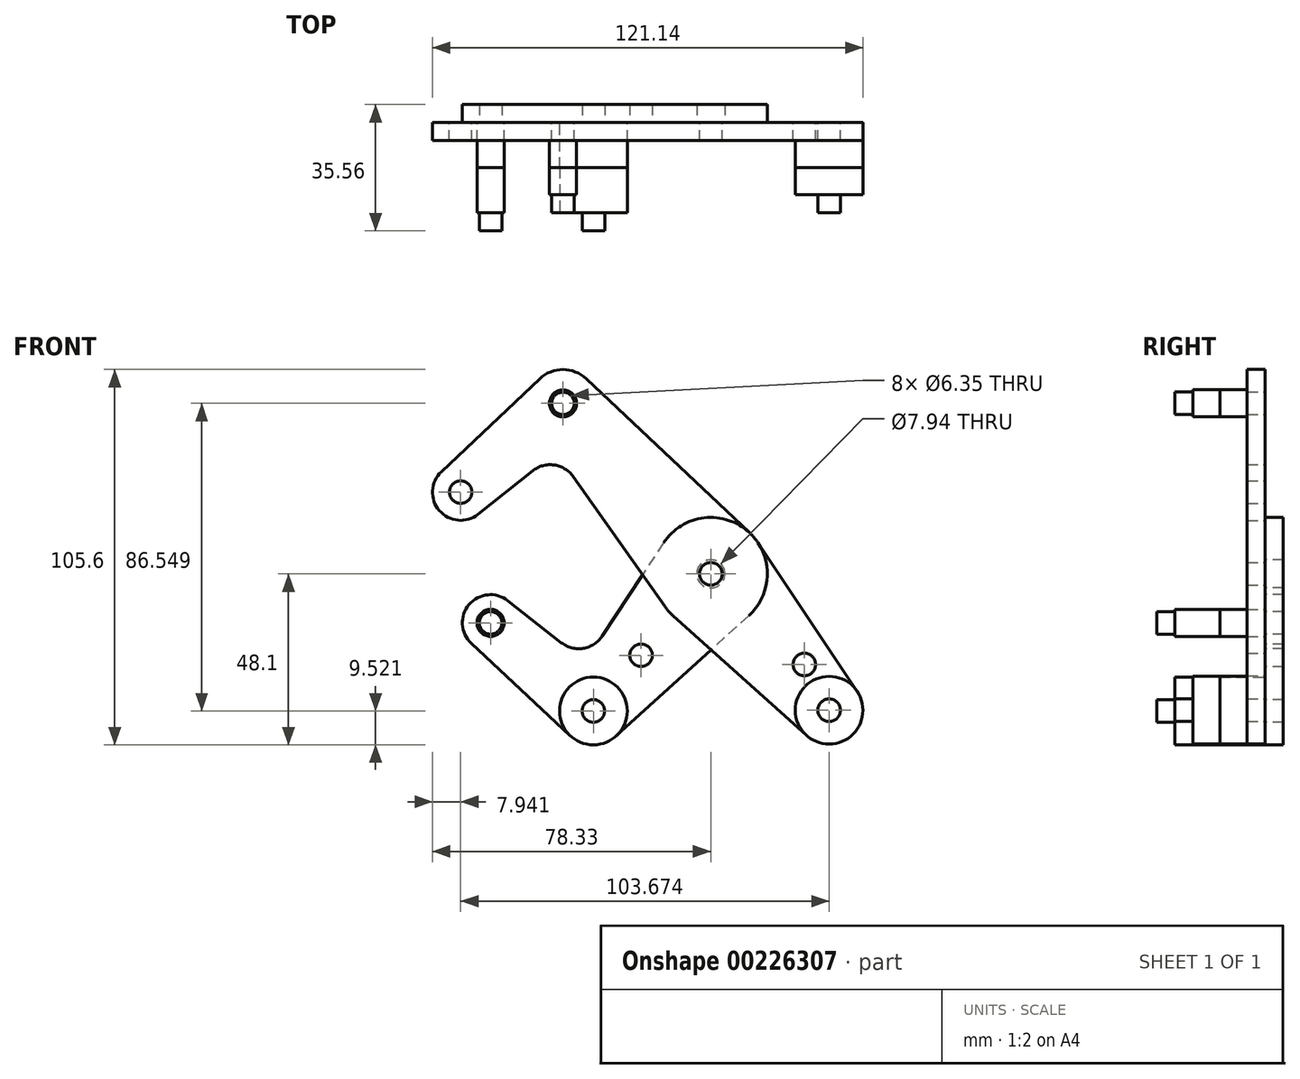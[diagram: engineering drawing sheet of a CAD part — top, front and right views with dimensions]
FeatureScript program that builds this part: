
annotation { "Feature Type Name" : "Feature", "Feature Type Description" : "" }
export const myFeature = defineFeature(function(context is Context, id is Id, definition is map)
    precondition{}
    {
        {
            var Q0;
            Q0=qCreatedBy(makeId("Front.planeOp"),FACE);
            var sketch = newSketch(context, id + "F0", { "sketchPlane" : qUnion([Q0])});
            skLineSegment(sketch, "E0", {"start": v(-41.6, 47.97) * mm, "end": v(41.6, -47.97) * mm, "construction": true});
            skCircle(sketch, "E1", {"center": v(0, 0) * mm, "radius": 3.18 * mm});
            skCircle(sketch, "E2", {"center": v(33.29, -38.38) * mm, "radius": 3.18 * mm});
            skCircle(sketch, "E3", {"center": v(-41.6, 47.97) * mm, "radius": 3.18 * mm});
            skCircle(sketch, "E4", {"center": v(-70.39, 23) * mm, "radius": 3.18 * mm});
            skLineSegment(sketch, "E5", {"start": v(-41.6, 47.97) * mm, "end": v(-70.39, 23) * mm, "construction": true});
            skCircle(sketch, "E6", {"center": v(33.29, -38.38) * mm, "radius": 9.53 * mm});
            skCircle(sketch, "E7", {"center": v(-70.39, 23) * mm, "radius": 7.94 * mm});
            skCircle(sketch, "E8", {"center": v(-41.6, 47.97) * mm, "radius": 9.53 * mm});
            skLineSegment(sketch, "E9", {"start": v(-75.83, 28.78) * mm, "end": v(-48.14, 54.9) * mm});
            skLineSegment(sketch, "E10", {"start": v(-65.44, 16.8) * mm, "end": v(-50.15, 28.98) * mm});
            skCircle(sketch, "E11", {"center": v(0, 0) * mm, "radius": 15.88 * mm});
            skLineSegment(sketch, "E12", {"start": v(-35.07, 54.9) * mm, "end": v(10.9, 11.55) * mm});
            skLineSegment(sketch, "E13", {"start": v(-38.72, 27.35) * mm, "end": v(-12.97, -9.15) * mm});
            skLineSegment(sketch, "E14", {"start": v(-10.6, -11.82) * mm, "end": v(26.93, -45.47) * mm});
            skLineSegment(sketch, "E15", {"start": v(13.2, 8.82) * mm, "end": v(41.2, -33.08) * mm});
            skArc(sketch, "E16.filletArc", {"start": v(-38.72, 27.35) * mm, "mid": v(-44.08, 30.63) * mm, "end": v(-50.15, 28.98) * mm});
            skLineSegment(sketch, "E17", {"start": v(0, 0) * mm, "end": v(-33.05, -38.58) * mm, "construction": true});
            skLineSegment(sketch, "E18", {"start": v(-33.05, -38.58) * mm, "end": v(-61.98, -13.8) * mm, "construction": true});
            skCircle(sketch, "E19", {"center": v(-61.98, -13.8) * mm, "radius": 3.18 * mm});
            skCircle(sketch, "E20", {"center": v(-33.05, -38.58) * mm, "radius": 3.18 * mm});
            skCircle(sketch, "E21", {"center": v(-61.98, -13.8) * mm, "radius": 7.94 * mm});
            skCircle(sketch, "E22", {"center": v(-33.05, -38.58) * mm, "radius": 9.53 * mm});
            skLineSegment(sketch, "E23", {"start": v(-57.08, -7.55) * mm, "end": v(-42.08, -19.35) * mm});
            skLineSegment(sketch, "E24", {"start": v(-67.4, -19.6) * mm, "end": v(-39.54, -45.55) * mm});
            skLineSegment(sketch, "E25", {"start": v(-13.25, 8.74) * mm, "end": v(-30.55, -17.48) * mm});
            skLineSegment(sketch, "E26", {"start": v(10.67, -11.75) * mm, "end": v(-26.65, -45.63) * mm});
            skArc(sketch, "E27.filletArc", {"start": v(-42.08, -19.35) * mm, "mid": v(-35.9, -20.95) * mm, "end": v(-30.55, -17.48) * mm});
            skCircle(sketch, "E28", {"center": v(-19.62, -22.9) * mm, "radius": 3.18 * mm});
            skCircle(sketch, "E29", {"center": v(26.32, -25.5) * mm, "radius": 3.18 * mm});
            skLineSegment(sketch, "E30", {"start": v(26.32, -25.5) * mm, "end": v(23.92, -27.58) * mm, "construction": true});
            skCircle(sketch, "E31", {"center": v(0, 0) * mm, "radius": 3.97 * mm});
            skSolve(sketch);
        }
        {
            var Q0;
            Q0=qCreatedBy(makeId("Front.planeOp"),FACE);
            cPlane(context, id + "F1", {"entities" : qUnion([Q0]), "cplaneType" : CPlaneType.OFFSET, "offset" : 12.7 * mm, "width" : 254 * mm, "height" : 254 * mm});
        }
        {
            var Q0;
            {var subQ1=sQuery(id+"F0.wireOp",EDGE,"E9");Q0=makeQuery(id+"F0.imprint","IMPRINT",FACE,{"disambiguationData":[TD([[makeQuery(id+"F0.imprint","IMPRINT",EDGE,{"derivedFrom":subQ1}),-1.0]])]});}
            var Q1;
            {var subQ0=sQuery(id+"F0.wireOp",EDGE,"E15");Q1=makeQuery(id+"F0.imprint","IMPRINT",FACE,{"disambiguationData":[TD([[makeQuery(id+"F0.imprint","IMPRINT",EDGE,{"derivedFrom":subQ0}),-1.0]])]});}
            var Q2;
            Q2=makeQuery(id+"F0.imprint","IMPRINT",FACE,{"disambiguationData":[TD([[makeQuery(id+"F0.imprint","IMPRINT",EDGE,{"derivedFrom":sQuery(id+"F0.wireOp",EDGE,"E2")}),-1.0]])]});
            var Q3;
            Q3=makeQuery(id+"F0.imprint","IMPRINT",FACE,{"disambiguationData":[TD([[makeQuery(id+"F0.imprint","IMPRINT",EDGE,{"derivedFrom":sQuery(id+"F0.wireOp",EDGE,"E31")}),-1.0]])]});
            var Q4;
            Q4=makeQuery(id+"F0.imprint","IMPRINT",FACE,{"disambiguationData":[TD([[makeQuery(id+"F0.imprint","IMPRINT",EDGE,{"derivedFrom":sQuery(id+"F0.wireOp",EDGE,"E3")}),-1.0]])]});
            var Q5;
            Q5=makeQuery(id+"F0.imprint","IMPRINT",FACE,{"disambiguationData":[TD([[makeQuery(id+"F0.imprint","IMPRINT",EDGE,{"derivedFrom":sQuery(id+"F0.wireOp",EDGE,"E4")}),-1.0]])]});
            var Q6;
            Q6=makeQuery(id+"F0.imprint","IMPRINT",FACE,{"disambiguationData":[TD([[makeQuery(id+"F0.imprint","IMPRINT",EDGE,{"derivedFrom":sQuery(id+"F0.wireOp",EDGE,"E1")}),-1.0]])]});
            var Q7;
            {var subQ0=sQuery(id+"F0.wireOp",EDGE,"E13");var subQ1=sQuery(id+"F0.wireOp",EDGE,"E11");var subQ2=makeQuery(id+"F0.imprint","INTERSECT",VERTEX,{"derivedFrom":[subQ1,subQ0]});Q7=makeQuery(id+"F0.imprint","IMPRINT",FACE,{"disambiguationData":[TD([[makeQuery(id+"F0.imprint","IMPRINT",EDGE,{"disambiguationData":[TD([[subQ2,1.0]])],"derivedFrom":subQ1}),-1.0]])]});}
            var Q8;
            {var subQ0=sQuery(id+"F0.wireOp",EDGE,"E14");var subQ1=sQuery(id+"F0.wireOp",EDGE,"E11");var subQ2=makeQuery(id+"F0.imprint","INTERSECT",VERTEX,{"derivedFrom":[subQ1,subQ0]});Q8=makeQuery(id+"F0.imprint","IMPRINT",FACE,{"disambiguationData":[TD([[makeQuery(id+"F0.imprint","IMPRINT",EDGE,{"disambiguationData":[TD([[subQ2,-1.0]])],"derivedFrom":subQ1}),-1.0]])]});}
            extrude(context, id + "F2", {"entities" : qUnion([Q0, Q1, Q2, Q3, Q4, Q5, Q6, Q7, Q8]), "depth" : 5.08 * mm});
        }
        {
            var Q0;
            {var subQ10=sQuery(id+"F0.wireOp",EDGE,"E23");Q0=makeQuery(id+"F0.imprint","IMPRINT",FACE,{"disambiguationData":[TD([[makeQuery(id+"F0.imprint","IMPRINT",EDGE,{"derivedFrom":subQ10}),-1.0]])]});}
            var Q1;
            Q1=makeQuery(id+"F0.imprint","IMPRINT",FACE,{"disambiguationData":[TD([[makeQuery(id+"F0.imprint","IMPRINT",EDGE,{"derivedFrom":sQuery(id+"F0.wireOp",EDGE,"E31")}),-1.0]])]});
            var Q2;
            {var subQ0=sQuery(id+"F0.wireOp",EDGE,"E13");var subQ1=sQuery(id+"F0.wireOp",EDGE,"E11");var subQ2=makeQuery(id+"F0.imprint","INTERSECT",VERTEX,{"derivedFrom":[subQ1,subQ0]});Q2=makeQuery(id+"F0.imprint","IMPRINT",FACE,{"disambiguationData":[TD([[makeQuery(id+"F0.imprint","IMPRINT",EDGE,{"disambiguationData":[TD([[subQ2,1.0]])],"derivedFrom":subQ1}),-1.0]])]});}
            var Q3;
            {var subQ0=sQuery(id+"F0.wireOp",EDGE,"E14");var subQ1=sQuery(id+"F0.wireOp",EDGE,"E11");var subQ2=makeQuery(id+"F0.imprint","INTERSECT",VERTEX,{"derivedFrom":[subQ1,subQ0]});Q3=makeQuery(id+"F0.imprint","IMPRINT",FACE,{"disambiguationData":[TD([[makeQuery(id+"F0.imprint","IMPRINT",EDGE,{"disambiguationData":[TD([[subQ2,-1.0]])],"derivedFrom":subQ1}),-1.0]])]});}
            var Q4;
            Q4=makeQuery(id+"F0.imprint","IMPRINT",FACE,{"disambiguationData":[TD([[makeQuery(id+"F0.imprint","IMPRINT",EDGE,{"derivedFrom":sQuery(id+"F0.wireOp",EDGE,"E20")}),-1.0]])]});
            var Q5;
            Q5=makeQuery(id+"F0.imprint","IMPRINT",FACE,{"disambiguationData":[TD([[makeQuery(id+"F0.imprint","IMPRINT",EDGE,{"derivedFrom":sQuery(id+"F0.wireOp",EDGE,"E19")}),-1.0]])]});
            extrude(context, id + "F3", {"entities" : qUnion([Q0, Q1, Q2, Q3, Q4, Q5]), "oppositeDirection" : true, "depth" : 5.08 * mm});
        }
        {
            var Q0;
            {var subQ1=sQuery(id+"F0.wireOp",EDGE,"E9");Q0=makeQuery(id+"F0.imprint","IMPRINT",FACE,{"disambiguationData":[TD([[makeQuery(id+"F0.imprint","IMPRINT",EDGE,{"derivedFrom":subQ1}),-1.0]])]});}
            var sketch = newSketch(context, id + "F4", { "sketchPlane" : qUnion([Q0])});
            skArc(sketch, "E32.0.0", {"start": v(26.93, -45.47) * mm, "mid": v(39.53, -45.57) * mm, "end": v(41.2, -33.08) * mm});
            skArc(sketch, "E32.0.1", {"start": v(41.2, -33.08) * mm, "mid": v(27.04, -31.18) * mm, "end": v(26.93, -45.47) * mm});
            skCircle(sketch, "E33", {"center": v(-41.6, 47.97) * mm, "radius": 3.81 * mm});
            skSolve(sketch);
        }
        {
            var Q0;
            Q0=makeQuery(id+"F3.opExtrude","CAP_FACE",FACE,{"disambiguationData":[OSD([sQuery(id+"F0.wireOp",EDGE,"E11"),sQuery(id+"F0.wireOp",EDGE,"E19"),sQuery(id+"F0.wireOp",EDGE,"E20"),sQuery(id+"F0.wireOp",EDGE,"E21"),sQuery(id+"F0.wireOp",EDGE,"E22"),sQuery(id+"F0.wireOp",EDGE,"E23"),sQuery(id+"F0.wireOp",EDGE,"E24"),sQuery(id+"F0.wireOp",EDGE,"E25"),sQuery(id+"F0.wireOp",EDGE,"E26"),sQuery(id+"F0.wireOp",EDGE,"E27.filletArc"),sQuery(id+"F0.wireOp",EDGE,"E28"),sQuery(id+"F0.wireOp",EDGE,"E31")])],"isStart":false});
            var sketch = newSketch(context, id + "F5", { "sketchPlane" : qUnion([Q0])});
            skCircle(sketch, "E34.0", {"center": v(33.05, -38.58) * mm, "radius": 9.53 * mm});
            skCircle(sketch, "E35", {"center": v(61.98, -13.8) * mm, "radius": 3.81 * mm});
            skSolve(sketch);
        }
        {
            var Q0;
            Q0 = qSketchRegion(id + "F4", true);
            var Q1;
            Q1 = qSketchRegion(id + "F5", true);
            var Q2;
            Q2=qCreatedBy(id+"F1.planeOp",FACE);
            extrude(context, id + "F6", {"entities" : qUnion([Q0, Q1]), "endBound" : BoundingType.UP_TO_SURFACE, "endBoundEntityFace" : qUnion([Q2]), "depth" : 25.4 * mm});
        }
        {
            var Q0;
            Q0=makeQuery(id+"F2.opExtrude","SWEPT_BODY",BODY,{"disambiguationData":[OSD([sQuery(id+"F0.wireOp",EDGE,"E1"),sQuery(id+"F0.wireOp",EDGE,"E2"),sQuery(id+"F0.wireOp",EDGE,"E3"),sQuery(id+"F0.wireOp",EDGE,"E4"),sQuery(id+"F0.wireOp",EDGE,"E6"),sQuery(id+"F0.wireOp",EDGE,"E7"),sQuery(id+"F0.wireOp",EDGE,"E8"),sQuery(id+"F0.wireOp",EDGE,"E9"),sQuery(id+"F0.wireOp",EDGE,"E10"),sQuery(id+"F0.wireOp",EDGE,"E11"),sQuery(id+"F0.wireOp",EDGE,"E12"),sQuery(id+"F0.wireOp",EDGE,"E13"),sQuery(id+"F0.wireOp",EDGE,"E14"),sQuery(id+"F0.wireOp",EDGE,"E15"),sQuery(id+"F0.wireOp",EDGE,"E16.filletArc"),sQuery(id+"F0.wireOp",EDGE,"E29")])]});
            var Q1;
            Q1=makeQuery(id+"F3.opExtrude","SWEPT_BODY",BODY,{"disambiguationData":[OSD([sQuery(id+"F0.wireOp",EDGE,"E11"),sQuery(id+"F0.wireOp",EDGE,"E19"),sQuery(id+"F0.wireOp",EDGE,"E20"),sQuery(id+"F0.wireOp",EDGE,"E21"),sQuery(id+"F0.wireOp",EDGE,"E22"),sQuery(id+"F0.wireOp",EDGE,"E23"),sQuery(id+"F0.wireOp",EDGE,"E24"),sQuery(id+"F0.wireOp",EDGE,"E25"),sQuery(id+"F0.wireOp",EDGE,"E26"),sQuery(id+"F0.wireOp",EDGE,"E27.filletArc"),sQuery(id+"F0.wireOp",EDGE,"E28"),sQuery(id+"F0.wireOp",EDGE,"E31")])]});
            var Q2;
            Q2=makeQuery(id+"F6.opExtrude","SWEPT_BODY",BODY,{"disambiguationData":[OSD([sQuery(id+"F4.wireOp",EDGE,"E33")])]});
            var Q3;
            Q3=makeQuery(id+"F6.opExtrude","SWEPT_BODY",BODY,{"disambiguationData":[OSD([sQuery(id+"F4.wireOp",EDGE,"E32.0.0"),sQuery(id+"F4.wireOp",EDGE,"E32.0.1")])]});
            var Q4;
            Q4=makeQuery(id+"F6.opExtrude","SWEPT_BODY",BODY,{"disambiguationData":[OSD([sQuery(id+"F5.wireOp",EDGE,"E34.0")])]});
            var Q5;
            Q5=makeQuery(id+"F6.opExtrude","SWEPT_BODY",BODY,{"disambiguationData":[OSD([sQuery(id+"F5.wireOp",EDGE,"E35")])]});
            booleanBodies(context, id + "F7", {"operationType" : BooleanOperationType.SUBTRACTION, "tools" : qUnion([Q0, Q1]), "targets" : qUnion([Q2, Q3, Q4, Q5]), "keepTools" : true});
        }
        {
            var Q0;
            Q0=makeQuery(id+"F6.opExtrude","SWEPT_BODY",BODY,{"disambiguationData":[OSD([sQuery(id+"F4.wireOp",EDGE,"E33")])]});
            var Q1;
            Q1=makeQuery(id+"F6.opExtrude","SWEPT_BODY",BODY,{"disambiguationData":[OSD([sQuery(id+"F4.wireOp",EDGE,"E32.0.0"),sQuery(id+"F4.wireOp",EDGE,"E32.0.1")])]});
            var Q2;
            Q2=makeQuery(id+"F6.opExtrude","SWEPT_BODY",BODY,{"disambiguationData":[OSD([sQuery(id+"F5.wireOp",EDGE,"E35")])]});
            var Q3;
            Q3=makeQuery(id+"F6.opExtrude","SWEPT_BODY",BODY,{"disambiguationData":[OSD([sQuery(id+"F5.wireOp",EDGE,"E34.0")])]});
            var Q4;
            Q4=qCreatedBy(id+"F1.planeOp",FACE);
            mirror(context, id + "F8", {"entities" : qUnion([Q0, Q1, Q2, Q3]), "mirrorPlane" : qUnion([Q4])});
        }
    });
